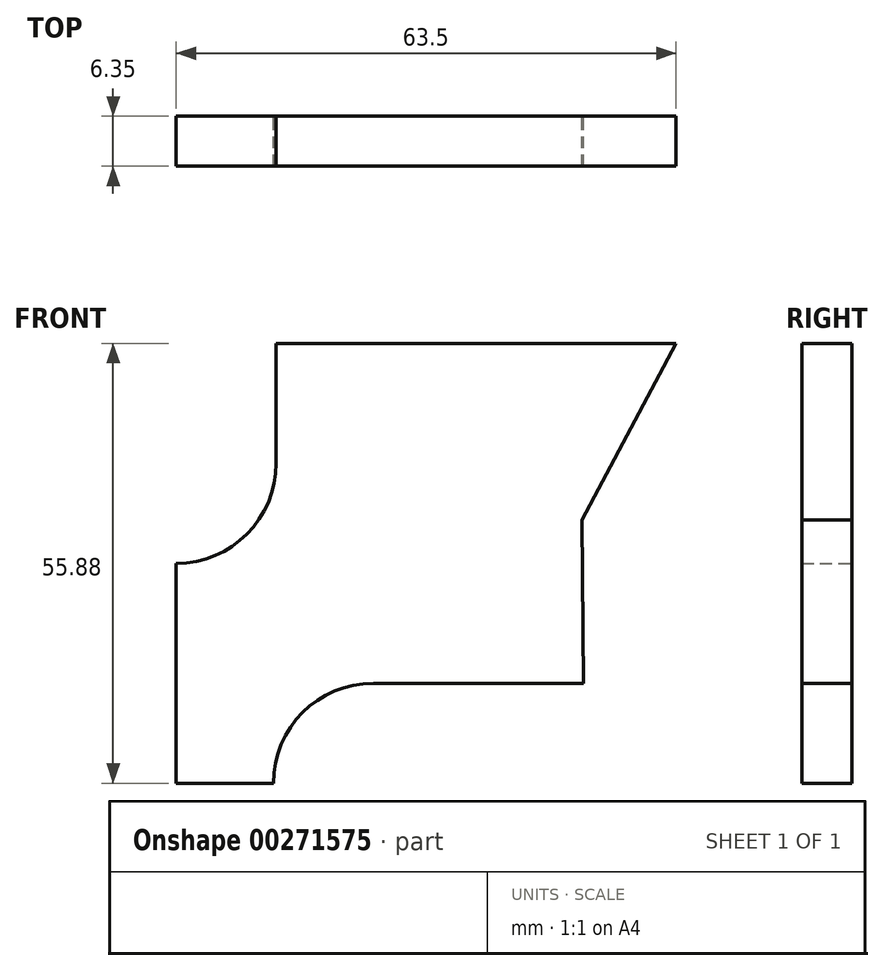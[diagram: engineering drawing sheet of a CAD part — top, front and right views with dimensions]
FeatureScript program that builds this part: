
annotation { "Feature Type Name" : "Feature", "Feature Type Description" : "" }
export const myFeature = defineFeature(function(context is Context, id is Id, definition is map)
    precondition{}
    {
        {
            var Q0;
            Q0=qCreatedBy(makeId("Front.planeOp"),FACE);
            var sketch = newSketch(context, id + "F0", { "sketchPlane" : qUnion([Q0])});
            skLineSegment(sketch, "E0", {"start": v(0, 0) * mm, "end": v(12.34, 0) * mm});
            skLineSegment(sketch, "E1", {"start": v(12.34, 0) * mm, "end": v(12.34, 0) * mm});
            skLineSegment(sketch, "E2", {"start": v(25.04, 12.7) * mm, "end": v(51.71, 12.7) * mm});
            skPoint(sketch, "E3.visualSharp", {"position": v(12.34, 12.7) * mm});
            skArc(sketch, "E3.filletArc", {"start": v(25.04, 12.7) * mm, "mid": v(16.06, 8.98) * mm, "end": v(12.34, 0) * mm});
            skLineSegment(sketch, "E4", {"start": v(0, 0) * mm, "end": v(0, 27.94) * mm});
            skLineSegment(sketch, "E5", {"start": v(0, 27.94) * mm, "end": v(0, 27.94) * mm});
            skLineSegment(sketch, "E6", {"start": v(12.7, 40.64) * mm, "end": v(12.7, 55.88) * mm});
            skLineSegment(sketch, "E7", {"start": v(12.7, 55.88) * mm, "end": v(63.5, 55.88) * mm});
            skPoint(sketch, "E8.visualSharp", {"position": v(12.7, 27.94) * mm});
            skArc(sketch, "E8.filletArc", {"start": v(0, 27.94) * mm, "mid": v(8.98, 31.66) * mm, "end": v(12.7, 40.64) * mm});
            skLineSegment(sketch, "E9", {"start": v(51.58, 33.45) * mm, "end": v(63.5, 55.88) * mm});
            skLineSegment(sketch, "E10", {"start": v(51.58, 33.45) * mm, "end": v(51.71, 12.7) * mm});
            skSolve(sketch);
        }
        {
            var Q0;
            Q0=makeQuery(id+"F0.imprint","IMPRINT",FACE,{"disambiguationData":[TD([[makeQuery(id+"F0.imprint","IMPRINT",EDGE,{"derivedFrom":sQuery(id+"F0.wireOp",EDGE,"E0")}),1.0]])]});
            extrude(context, id + "F1", {"entities" : qUnion([Q0]), "depth" : 6.35 * mm});
        }
    });
